# Revit family: 353_House Well SOK 315_1000
name_source: partatom
category: Plumbing Fixtures
units: mm (PartAtom-declared; Revit-internal decimal feet)

## family parameters
Always vertical = Yes
Cut with Voids When Loaded = No
Part Type = Normal
Room Calculation Point = No
Round Connector Dimension = Use Diameter
Shared = No
Work Plane-Based = No

## types (1)
- Drainage inspection chamber 315 p/n 086251
    BD = 315 mm  [stored 1.03346 ft]
    CAT0 = Yes
    CLBTZ = 0 mm  [stored 0 ft]
    CL_Location_5000 = 5000 mm  [stored 16.4042 ft]
    D = 110 mm
    D1 = 110 mm
    D2 = 110 mm
    DP2 = 66 mm
    DP2__ve = -66 mm
    Description = Drainage inspection chamber 315 p/n:086251
    MC Product Code = Drainage inspection chamber 315 p/n:086251
    Manufacturer = Pipelife
    QmdConnectorList = 651;D;652;D1;653;D2
    R = 55 mm  [stored 0.180446 ft]
    R2 = 55 mm  [stored 0.180446 ft]
    URL = http://www.pipelife.fi
    X1 = 203 mm  [stored 0.66601 ft]
    Z1 = 255 mm  [stored 0.836614 ft]
    Z1__ve = -255 mm  [stored -0.836614 ft]
    magiPartTypeId = 353
    magiProductFamilyId = House Well SOK 315/1000
    magiProductId = House Well SOK 315/1000

note: [stored X ft] marks values corroborated as IEEE doubles in the binary element streams (Revit-internal decimal feet)

## geometry (parser evidence)
native form markers: Sweep x2
no freeform markers — native parametric forms only
